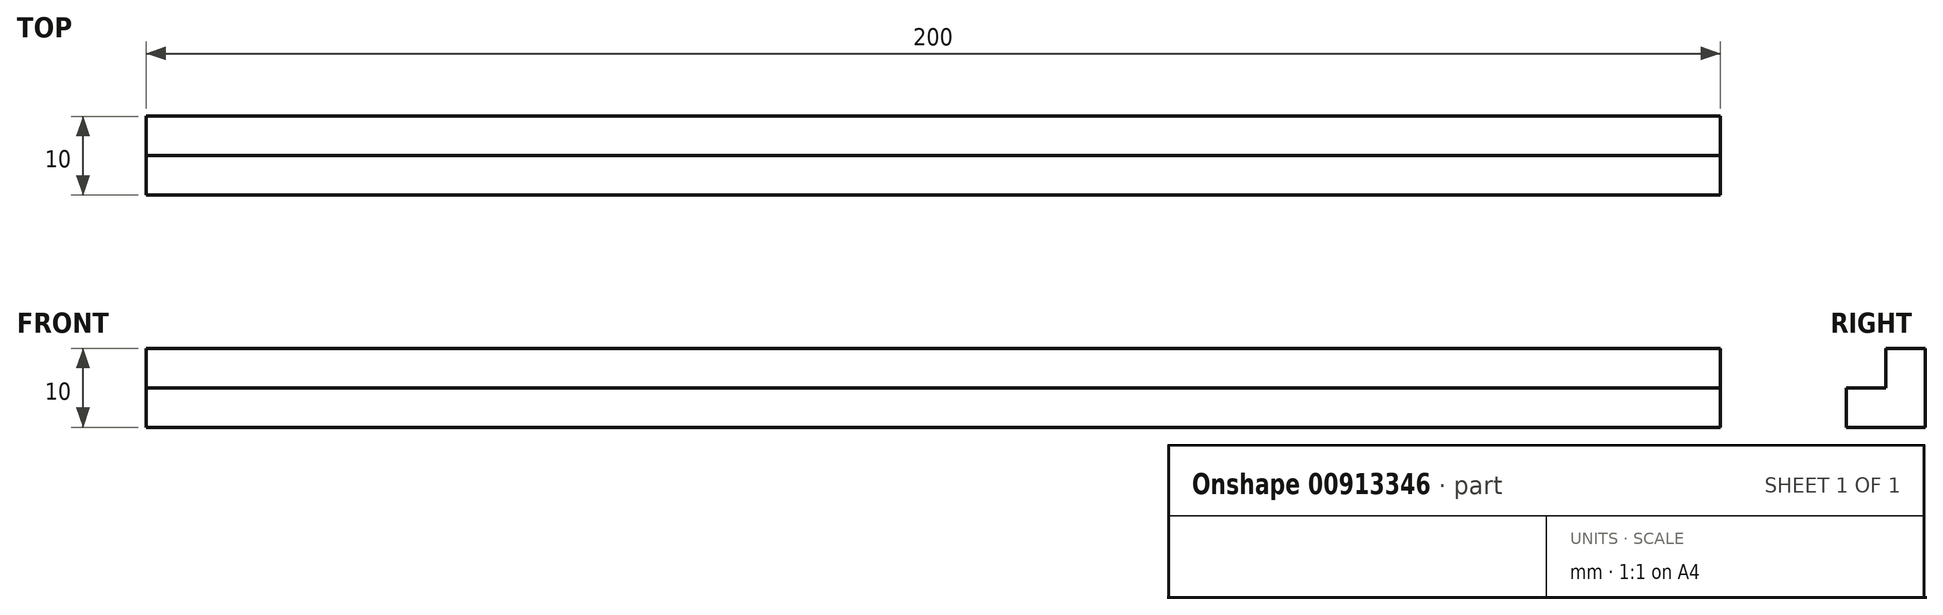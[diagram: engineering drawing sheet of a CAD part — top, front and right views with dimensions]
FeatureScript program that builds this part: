
annotation { "Feature Type Name" : "Feature", "Feature Type Description" : "" }
export const myFeature = defineFeature(function(context is Context, id is Id, definition is map)
    precondition{}
    {
        {
            var Q0;
            Q0=qCreatedBy(makeId("Top.planeOp"),FACE);
            var sketch = newSketch(context, id + "F0", { "sketchPlane" : qUnion([Q0])});
            skLineSegment(sketch, "E0.bottom", {"start": v(-146.9, 24.3) * mm, "end": v(53.1, 24.3) * mm});
            skLineSegment(sketch, "E0.top", {"start": v(-146.9, 14.3) * mm, "end": v(53.1, 14.3) * mm});
            skLineSegment(sketch, "E0.left", {"start": v(-146.9, 24.3) * mm, "end": v(-146.9, 14.3) * mm});
            skLineSegment(sketch, "E0.right", {"start": v(53.1, 24.3) * mm, "end": v(53.1, 14.3) * mm});
            skSolve(sketch);
        }
        {
            var Q0;
            Q0=makeQuery(id+"F0.imprint","IMPRINT",FACE,{"disambiguationData":[TD([[makeQuery(id+"F0.imprint","IMPRINT",EDGE,{"derivedFrom":sQuery(id+"F0.wireOp",EDGE,"E0.bottom")}),-1.0]])]});
            extrude(context, id + "F1", {"entities" : qUnion([Q0]), "depth" : 10 * mm, "offsetDistance" : 25 * mm});
        }
        {
            var Q0;
            Q0=makeQuery(id+"F1.opExtrude","SWEPT_FACE",FACE,{"disambiguationData":[OSD([sQuery(id+"F0.wireOp",EDGE,"E0.right")])]});
            var sketch = newSketch(context, id + "F2", { "sketchPlane" : qUnion([Q0])});
            skLineSegment(sketch, "E1.bottom", {"start": v(14.3, 10) * mm, "end": v(19.3, 10) * mm});
            skLineSegment(sketch, "E1.top", {"start": v(14.3, 5) * mm, "end": v(19.3, 5) * mm});
            skLineSegment(sketch, "E1.left", {"start": v(14.3, 10) * mm, "end": v(14.3, 5) * mm});
            skLineSegment(sketch, "E1.right", {"start": v(19.3, 10) * mm, "end": v(19.3, 5) * mm});
            skSolve(sketch);
        }
        {
            var Q0;
            Q0 = qSketchRegion(id + "F2", true);
            extrude(context, id + "F3", {"entities" : qUnion([Q0]), "operationType" : NewBodyOperationType.REMOVE, "oppositeDirection" : true, "depth" : 300 * mm, "offsetDistance" : 25 * mm});
        }
    });
